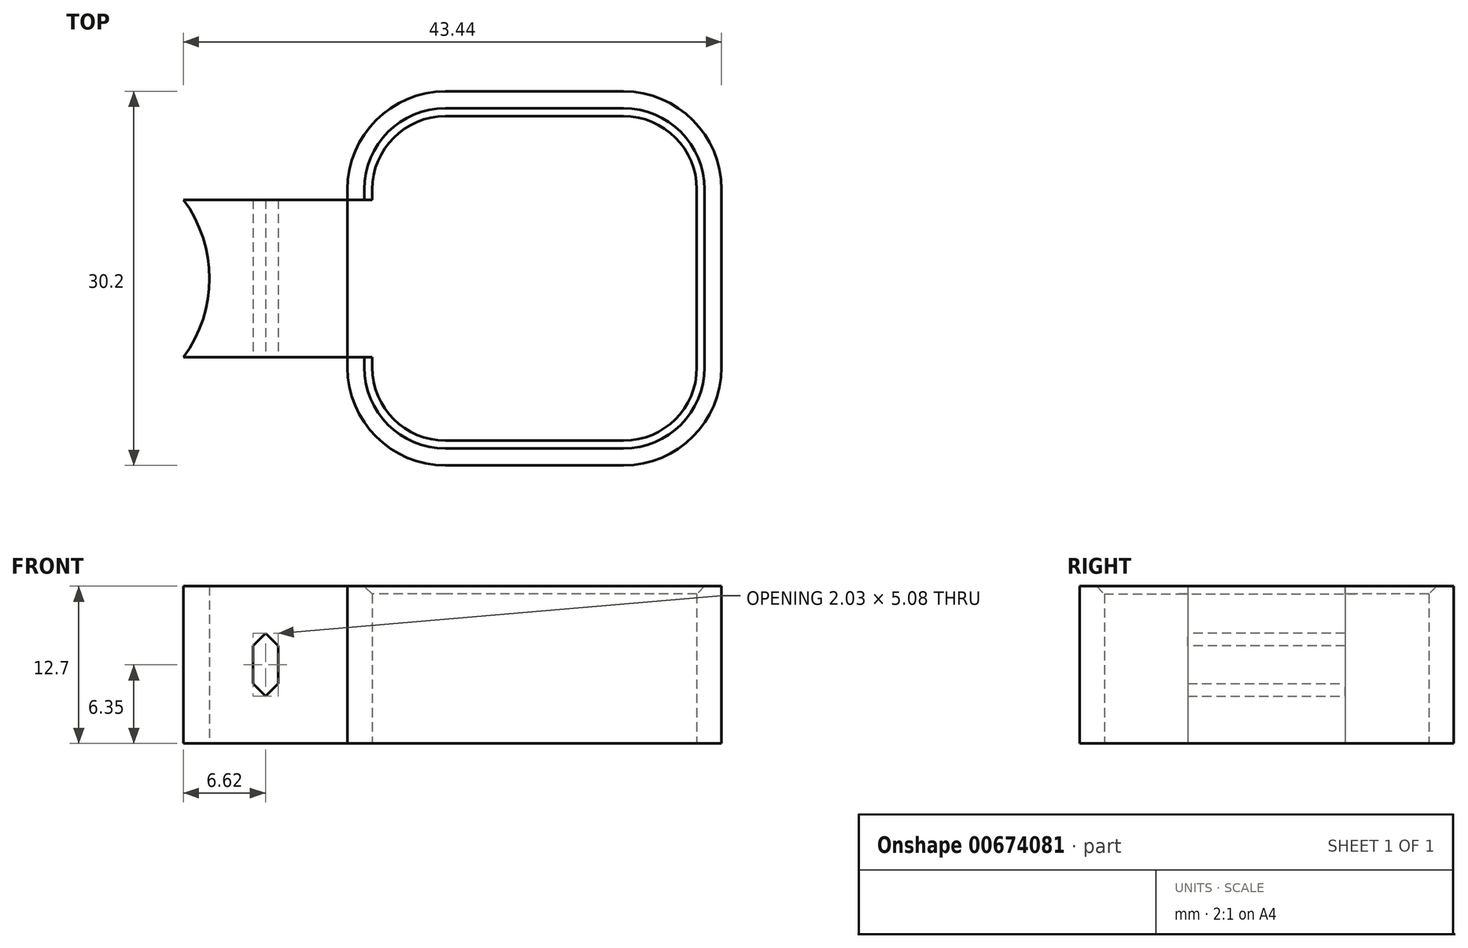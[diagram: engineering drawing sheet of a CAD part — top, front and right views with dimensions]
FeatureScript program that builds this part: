
annotation { "Feature Type Name" : "Feature", "Feature Type Description" : "" }
export const myFeature = defineFeature(function(context is Context, id is Id, definition is map)
    precondition{}
    {
        {
            var Q0;
            Q0=qCreatedBy(makeId("Top.planeOp"),FACE);
            var sketch = newSketch(context, id + "F0", { "sketchPlane" : qUnion([Q0])});
            skCircle(sketch, "E0.cCircle", {"center": v(0, 0) * mm, "radius": 11 * mm, "construction": true});
            skLineSegment(sketch, "E0.0", {"start": v(-7.2, 11) * mm, "end": v(7.2, 11) * mm, "construction": true});
            skLineSegment(sketch, "E0.1", {"start": v(11, 7.2) * mm, "end": v(11, -7.2) * mm, "construction": true});
            skLineSegment(sketch, "E0.2", {"start": v(7.2, -11) * mm, "end": v(-7.2, -11) * mm, "construction": true});
            skLineSegment(sketch, "E0.3", {"start": v(-11, -7.2) * mm, "end": v(-11, 7.2) * mm, "construction": true});
            skPoint(sketch, "E0.0.midPoint", {"position": v(0, 11) * mm});
            skPoint(sketch, "E1.visualSharp", {"position": v(-11, 11) * mm});
            skArc(sketch, "E1.filletArc", {"start": v(-7.19, 11) * mm, "mid": v(-9.88, 9.88) * mm, "end": v(-11, 7.2) * mm, "construction": true});
            skPoint(sketch, "E2.visualSharp", {"position": v(11, 11) * mm});
            skArc(sketch, "E2.filletArc", {"start": v(11, 7.2) * mm, "mid": v(9.88, 9.88) * mm, "end": v(7.2, 11) * mm, "construction": true});
            skPoint(sketch, "E3.visualSharp", {"position": v(11, -11) * mm});
            skArc(sketch, "E3.filletArc", {"start": v(7.2, -11) * mm, "mid": v(9.88, -9.88) * mm, "end": v(11, -7.2) * mm, "construction": true});
            skPoint(sketch, "E4.visualSharp", {"position": v(-11, -11) * mm});
            skArc(sketch, "E4.filletArc", {"start": v(-11, -7.2) * mm, "mid": v(-9.88, -9.88) * mm, "end": v(-7.2, -11) * mm, "construction": true});
            skLineSegment(sketch, "E5.0", {"start": v(13.1, 7.2) * mm, "end": v(13.1, -7.2) * mm});
            skArc(sketch, "E5.1", {"start": v(7.2, -13.1) * mm, "mid": v(11.37, -11.37) * mm, "end": v(13.1, -7.2) * mm});
            skArc(sketch, "E5.2", {"start": v(13.1, 7.2) * mm, "mid": v(11.37, 11.37) * mm, "end": v(7.2, 13.1) * mm});
            skLineSegment(sketch, "E5.3", {"start": v(7.2, -13.1) * mm, "end": v(-7.2, -13.1) * mm});
            skLineSegment(sketch, "E5.4", {"start": v(-7.2, 13.1) * mm, "end": v(7.2, 13.1) * mm});
            skArc(sketch, "E5.5", {"start": v(-7.2, 13.1) * mm, "mid": v(-11.37, 11.37) * mm, "end": v(-13.1, 7.2) * mm});
            skLineSegment(sketch, "E5.6", {"start": v(-13.1, -7.2) * mm, "end": v(-13.1, 7.2) * mm});
            skArc(sketch, "E5.7", {"start": v(-13.1, -7.2) * mm, "mid": v(-11.37, -11.37) * mm, "end": v(-7.2, -13.1) * mm});
            skArc(sketch, "E6.0", {"start": v(-7.2, 15.1) * mm, "mid": v(-12.78, 12.78) * mm, "end": v(-15.1, 7.2) * mm});
            skLineSegment(sketch, "E6.1", {"start": v(-15.1, -7.2) * mm, "end": v(-15.1, 7.2) * mm});
            skLineSegment(sketch, "E6.2", {"start": v(-7.2, 15.1) * mm, "end": v(7.2, 15.1) * mm});
            skArc(sketch, "E6.3", {"start": v(-15.1, -7.2) * mm, "mid": v(-12.78, -12.78) * mm, "end": v(-7.2, -15.1) * mm});
            skArc(sketch, "E6.4", {"start": v(15.1, 7.2) * mm, "mid": v(12.78, 12.78) * mm, "end": v(7.2, 15.1) * mm});
            skLineSegment(sketch, "E6.5", {"start": v(15.1, 7.2) * mm, "end": v(15.1, -7.2) * mm});
            skArc(sketch, "E6.6", {"start": v(7.2, -15.1) * mm, "mid": v(12.78, -12.78) * mm, "end": v(15.1, -7.2) * mm});
            skLineSegment(sketch, "E6.7", {"start": v(7.2, -15.1) * mm, "end": v(-7.2, -15.1) * mm});
            skCircle(sketch, "E7", {"center": v(-36.91, 0) * mm, "radius": 10.67 * mm});
            skLineSegment(sketch, "E8.bottom", {"start": v(-13.1, -6.35) * mm, "end": v(-28.34, -6.35) * mm});
            skLineSegment(sketch, "E8.top", {"start": v(-13.1, 6.35) * mm, "end": v(-28.34, 6.35) * mm});
            skLineSegment(sketch, "E8.left", {"start": v(-13.1, -6.35) * mm, "end": v(-13.1, 6.35) * mm});
            skLineSegment(sketch, "E8.right", {"start": v(-28.34, -6.35) * mm, "end": v(-28.34, 6.35) * mm});
            skSolve(sketch);
        }
        {
            var Q0;
            {var subQ0=sQuery(id+"F0.wireOp",EDGE,"E8.bottom");var subQ1=sQuery(id+"F0.wireOp",EDGE,"E6.1");var subQ2=makeQuery(id+"F0.imprint","INTERSECT",VERTEX,{"derivedFrom":[subQ1,subQ0]});Q0=makeQuery(id+"F0.imprint","IMPRINT",FACE,{"disambiguationData":[TD([[makeQuery(id+"F0.imprint","IMPRINT",EDGE,{"disambiguationData":[TD([[subQ2,-1.0]])],"derivedFrom":subQ1}),1.0]])]});}
            var Q1;
            {var subQ5=sQuery(id+"F0.wireOp",EDGE,"E8.left");Q1=makeQuery(id+"F0.imprint","IMPRINT",FACE,{"disambiguationData":[TD([[makeQuery(id+"F0.imprint","IMPRINT",EDGE,{"derivedFrom":subQ5}),1.0]])]});}
            var Q2;
            Q2=makeQuery(id+"F0.imprint","IMPRINT",FACE,{"disambiguationData":[TD([[makeQuery(id+"F0.imprint","IMPRINT",EDGE,{"derivedFrom":sQuery(id+"F0.wireOp",EDGE,"E5.0")}),1.0]])]});
            extrude(context, id + "F1", {"entities" : qUnion([Q0, Q1, Q2]), "depth" : 12.7 * mm, "offsetDistance" : 25.4 * mm});
        }
        {
            var Q0;
            Q0=makeQuery(id+"F1.opExtrude","CAP_EDGE",EDGE,{"disambiguationData":[OSD([sQuery(id+"F0.wireOp",EDGE,"E5.5")])],"isStart":false});
            var Q1;
            Q1=makeQuery(id+"F1.opExtrude","CAP_EDGE",EDGE,{"disambiguationData":[OSD([sQuery(id+"F0.wireOp",EDGE,"E5.4")])],"isStart":false});
            var Q2;
            Q2=makeQuery(id+"F1.opExtrude","CAP_EDGE",EDGE,{"disambiguationData":[OSD([sQuery(id+"F0.wireOp",EDGE,"E5.2")])],"isStart":false});
            var Q3;
            Q3=makeQuery(id+"F1.opExtrude","CAP_EDGE",EDGE,{"disambiguationData":[OSD([sQuery(id+"F0.wireOp",EDGE,"E5.0")])],"isStart":false});
            var Q4;
            Q4=makeQuery(id+"F1.opExtrude","CAP_EDGE",EDGE,{"disambiguationData":[OSD([sQuery(id+"F0.wireOp",EDGE,"E5.1")])],"isStart":false});
            var Q5;
            Q5=makeQuery(id+"F1.opExtrude","CAP_EDGE",EDGE,{"disambiguationData":[OSD([sQuery(id+"F0.wireOp",EDGE,"E5.3")])],"isStart":false});
            var Q6;
            Q6=makeQuery(id+"F1.opExtrude","CAP_EDGE",EDGE,{"disambiguationData":[OSD([sQuery(id+"F0.wireOp",EDGE,"E5.7")])],"isStart":false});
            var Q7;
            Q7=makeQuery(id+"F1.opExtrude","CAP_EDGE",EDGE,{"disambiguationData":[OSD([sQuery(id+"F0.wireOp",EDGE,"E5.6"),sQuery(id+"F0.wireOp",EDGE,"E8.left")])],"isStart":false});
            chamfer(context, id + "F2", {"entities" : qUnion([Q0, Q1, Q2, Q3, Q4, Q5, Q6, Q7]), "width" : 0.64 * mm, "tangentPropagation" : true});
        }
        {
            var Q0;
            Q0=makeQuery(id+"F1.opExtrude","SWEPT_FACE",FACE,{"disambiguationData":[OSD([sQuery(id+"F0.wireOp",EDGE,"E8.bottom")])]});
            var sketch = newSketch(context, id + "F3", { "sketchPlane" : qUnion([Q0])});
            skLineSegment(sketch, "E9", {"start": v(-28.34, 6.35) * mm, "end": v(-15.1, 6.35) * mm, "construction": true});
            skLineSegment(sketch, "E10", {"start": v(-21.72, 0) * mm, "end": v(-21.72, 12.7) * mm, "construction": true});
            skPoint(sketch, "E11", {"position": v(-21.72, 6.35) * mm});
            skLineSegment(sketch, "E12.bottom", {"start": v(-22.74, 8.9) * mm, "end": v(-20.7, 8.9) * mm});
            skLineSegment(sketch, "E12.top", {"start": v(-22.74, 3.81) * mm, "end": v(-20.7, 3.81) * mm});
            skLineSegment(sketch, "E12.left", {"start": v(-22.74, 8.9) * mm, "end": v(-22.74, 3.81) * mm});
            skLineSegment(sketch, "E12.right", {"start": v(-20.7, 8.9) * mm, "end": v(-20.7, 3.81) * mm});
            skSolve(sketch);
        }
        {
            var Q0;
            Q0=makeQuery(id+"F3.imprint","IMPRINT",FACE,{"disambiguationData":[TD([[makeQuery(id+"F3.imprint","IMPRINT",EDGE,{"derivedFrom":sQuery(id+"F3.wireOp",EDGE,"E12.bottom")}),-1.0]])]});
            extrude(context, id + "F4", {"entities" : qUnion([Q0]), "operationType" : NewBodyOperationType.REMOVE, "oppositeDirection" : true, "depth" : 25.4 * mm, "offsetDistance" : 25.4 * mm});
        }
        {
            var Q0;
            Q0=makeQuery(id+"F4.boolean.opBoolean","COPY",EDGE,{"derivedFrom":makeQuery(id+"F4.opExtrude","SWEPT_EDGE",EDGE,{"disambiguationData":[OSD([sQuery(id+"F3.wireOp",EDGE,"E12.top"),sQuery(id+"F3.wireOp",EDGE,"E12.left")])]})});
            var Q1;
            Q1=makeQuery(id+"F4.boolean.opBoolean","COPY",EDGE,{"derivedFrom":makeQuery(id+"F4.opExtrude","SWEPT_EDGE",EDGE,{"disambiguationData":[OSD([sQuery(id+"F3.wireOp",EDGE,"E12.top"),sQuery(id+"F3.wireOp",EDGE,"E12.right")])]})});
            var Q2;
            Q2=makeQuery(id+"F4.boolean.opBoolean","COPY",EDGE,{"derivedFrom":makeQuery(id+"F4.opExtrude","SWEPT_EDGE",EDGE,{"disambiguationData":[OSD([sQuery(id+"F3.wireOp",EDGE,"E12.bottom"),sQuery(id+"F3.wireOp",EDGE,"E12.right")])]})});
            var Q3;
            Q3=makeQuery(id+"F4.boolean.opBoolean","COPY",EDGE,{"derivedFrom":makeQuery(id+"F4.opExtrude","SWEPT_EDGE",EDGE,{"disambiguationData":[OSD([sQuery(id+"F3.wireOp",EDGE,"E12.bottom"),sQuery(id+"F3.wireOp",EDGE,"E12.left")])]})});
            chamfer(context, id + "F5", {"entities" : qUnion([Q0, Q1, Q2, Q3]), "width" : 1.02 * mm, "tangentPropagation" : true});
        }
    });
